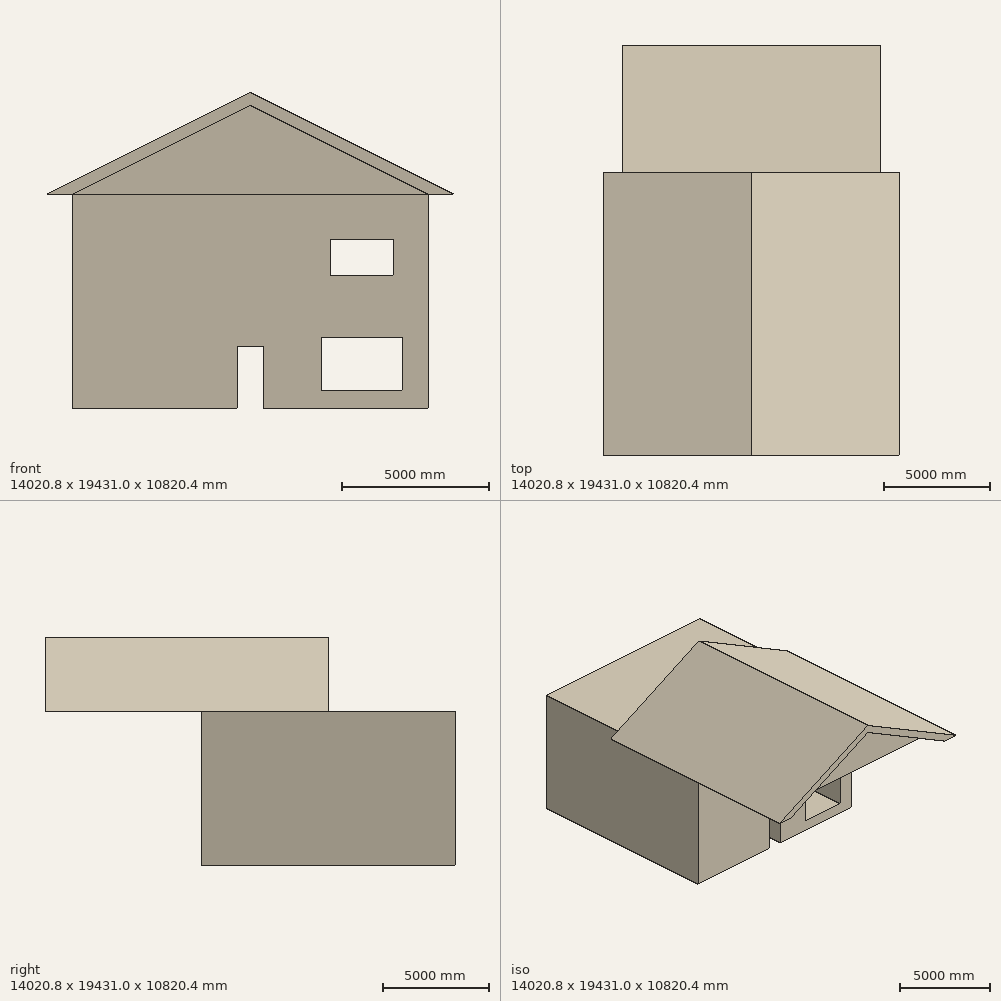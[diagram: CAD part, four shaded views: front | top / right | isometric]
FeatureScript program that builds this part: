
annotation { "Feature Type Name" : "Feature", "Feature Type Description" : "" }
export const myFeature = defineFeature(function(context is Context, id is Id, definition is map)
    precondition{}
    {
        {
            var Q0;
            Q0=qCreatedBy(makeId("Front.planeOp"),FACE);
            var sketch = newSketch(context, id + "F0", { "sketchPlane" : qUnion([Q0])});
            skLineSegment(sketch, "E0", {"start": v(0, 0) * mm, "end": v(-6096, 0) * mm});
            skLineSegment(sketch, "E1", {"start": v(0, 0) * mm, "end": v(6096, 0) * mm});
            skLineSegment(sketch, "E2", {"start": v(0, 0) * mm, "end": v(0, 3048) * mm, "construction": true});
            skLineSegment(sketch, "E3", {"start": v(0, 3048) * mm, "end": v(-6096, 0) * mm});
            skLineSegment(sketch, "E4", {"start": v(0, 3048) * mm, "end": v(6096, 0) * mm});
            skLineSegment(sketch, "E5", {"start": v(-6096, 0) * mm, "end": v(-7010.4, 0) * mm});
            skLineSegment(sketch, "E6", {"start": v(6096, 0) * mm, "end": v(7010.4, 0) * mm});
            skLineSegment(sketch, "E7", {"start": v(0, 3048) * mm, "end": v(0, 3505.2) * mm});
            skLineSegment(sketch, "E8", {"start": v(0, 3505.2) * mm, "end": v(-7010.4, 0) * mm});
            skLineSegment(sketch, "E9", {"start": v(0, 3505.2) * mm, "end": v(7010.4, 0) * mm});
            skLineSegment(sketch, "E10", {"start": v(-6096, 0) * mm, "end": v(-6096, -7315.2) * mm});
            skLineSegment(sketch, "E11", {"start": v(6096, 0) * mm, "end": v(6096, -7315.2) * mm});
            skLineSegment(sketch, "E12", {"start": v(-6096, -7315.2) * mm, "end": v(6096, -7315.2) * mm});
            skLineSegment(sketch, "E13", {"start": v(-6096, -7315.2) * mm, "end": v(-6096, -7620) * mm});
            skLineSegment(sketch, "E14", {"start": v(-6096, -7620) * mm, "end": v(6096, -7620) * mm});
            skLineSegment(sketch, "E15", {"start": v(6096, -7620) * mm, "end": v(6096, -7315.2) * mm});
            skLineSegment(sketch, "E16", {"start": v(0, -7315.2) * mm, "end": v(457.2, -7315.2) * mm});
            skLineSegment(sketch, "E17", {"start": v(0, -7315.2) * mm, "end": v(-457.2, -7315.2) * mm});
            skLineSegment(sketch, "E18", {"start": v(457.2, -7315.2) * mm, "end": v(457.2, -5181.6) * mm});
            skLineSegment(sketch, "E19", {"start": v(-457.2, -7315.2) * mm, "end": v(-457.2, -5181.6) * mm});
            skLineSegment(sketch, "E20", {"start": v(-457.2, -5181.6) * mm, "end": v(457.2, -5181.6) * mm});
            skLineSegment(sketch, "E21.bottom", {"start": v(2743.2, -5181.6) * mm, "end": v(4876.8, -5181.6) * mm});
            skLineSegment(sketch, "E21.top", {"start": v(2743.2, -6400.8) * mm, "end": v(4876.8, -6400.8) * mm});
            skLineSegment(sketch, "E21.left", {"start": v(2743.2, -5181.6) * mm, "end": v(2743.2, -6400.8) * mm});
            skLineSegment(sketch, "E21.right", {"start": v(4876.8, -5181.6) * mm, "end": v(4876.8, -6400.8) * mm});
            skLineSegment(sketch, "E22.0", {"start": v(2438.4, -4876.8) * mm, "end": v(5181.6, -4876.8) * mm});
            skLineSegment(sketch, "E22.1", {"start": v(2438.4, -4876.8) * mm, "end": v(2438.4, -6705.6) * mm});
            skLineSegment(sketch, "E22.2", {"start": v(2438.4, -6705.6) * mm, "end": v(5181.6, -6705.6) * mm});
            skLineSegment(sketch, "E22.3", {"start": v(5181.6, -4876.8) * mm, "end": v(5181.6, -6705.6) * mm});
            skLineSegment(sketch, "E23.bottom", {"start": v(2743.2, -1524) * mm, "end": v(4876.8, -1524) * mm});
            skLineSegment(sketch, "E23.top", {"start": v(2743.2, -2743.2) * mm, "end": v(4876.8, -2743.2) * mm});
            skLineSegment(sketch, "E23.left", {"start": v(2743.2, -1524) * mm, "end": v(2743.2, -2743.2) * mm});
            skLineSegment(sketch, "E23.right", {"start": v(4876.8, -1524) * mm, "end": v(4876.8, -2743.2) * mm});
            skLineSegment(sketch, "E24.0", {"start": v(2743.2, -1529) * mm, "end": v(4876.8, -1529) * mm});
            skLineSegment(sketch, "E25.0", {"start": v(4881.8, -1524) * mm, "end": v(4881.8, -2748.2) * mm});
            skLineSegment(sketch, "E25.1", {"start": v(2743.2, -2748.2) * mm, "end": v(4881.8, -2748.2) * mm});
            skSolve(sketch);
        }
        {
            var Q0;
            Q0=makeQuery(id+"F0.imprint","IMPRINT",FACE,{"disambiguationData":[TD([[makeQuery(id+"F0.imprint","IMPRINT",EDGE,{"derivedFrom":sQuery(id+"F0.wireOp",EDGE,"E4")}),1.0]])]});
            var Q1;
            Q1=makeQuery(id+"F0.imprint","IMPRINT",FACE,{"disambiguationData":[TD([[makeQuery(id+"F0.imprint","IMPRINT",EDGE,{"derivedFrom":sQuery(id+"F0.wireOp",EDGE,"E3")}),-1.0]])]});
            extrude(context, id + "F1", {"entities" : qUnion([Q0, Q1]), "depth" : 13411.2 * mm, "offsetDistance" : 30.48 * mm});
        }
        {
            var Q0;
            Q0=makeQuery(id+"F0.imprint","IMPRINT",FACE,{"disambiguationData":[TD([[makeQuery(id+"F0.imprint","IMPRINT",EDGE,{"derivedFrom":sQuery(id+"F0.wireOp",EDGE,"E0")}),-1.0]])]});
            extrude(context, id + "F2", {"entities" : qUnion([Q0]), "operationType" : NewBodyOperationType.ADD, "depth" : 12192 * mm, "offsetDistance" : 30.48 * mm});
        }
        {
            var Q0;
            Q0=makeQuery(id+"F0.imprint","IMPRINT",FACE,{"disambiguationData":[TD([[makeQuery(id+"F0.imprint","IMPRINT",EDGE,{"derivedFrom":sQuery(id+"F0.wireOp",EDGE,"E0")}),1.0]])]});
            extrude(context, id + "F3", {"entities" : qUnion([Q0]), "operationType" : NewBodyOperationType.ADD, "endBound" : BoundingType.SYMMETRIC, "depth" : 12039.6 * mm, "offsetDistance" : 30.48 * mm});
        }
    });
